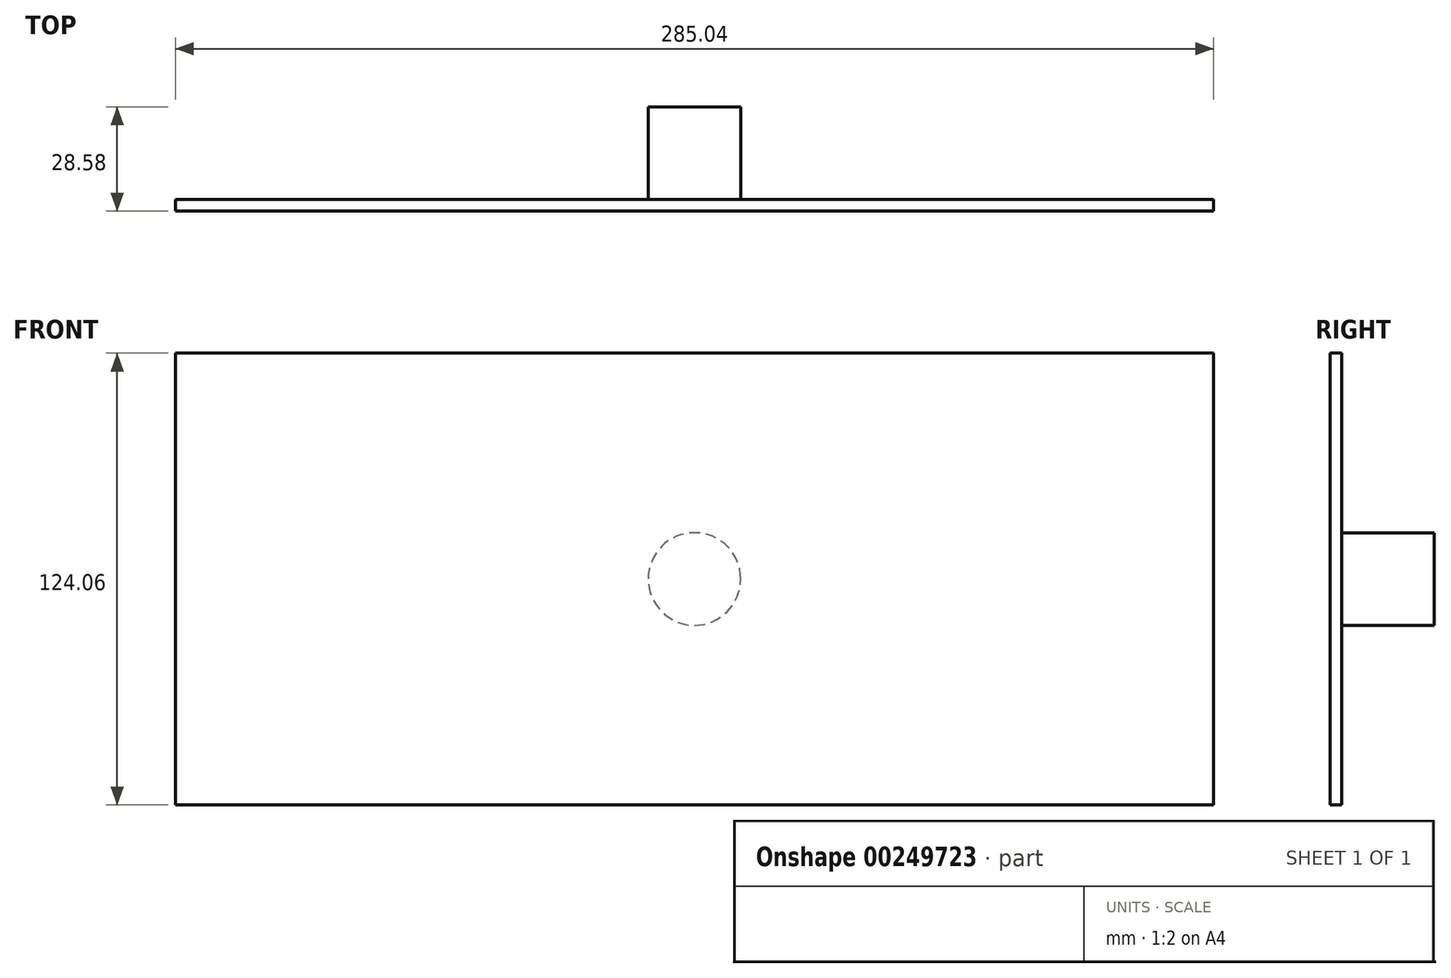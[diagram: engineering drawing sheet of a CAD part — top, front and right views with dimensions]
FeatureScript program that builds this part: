
annotation { "Feature Type Name" : "Feature", "Feature Type Description" : "" }
export const myFeature = defineFeature(function(context is Context, id is Id, definition is map)
    precondition{}
    {
        {
            var Q0;
            Q0=qCreatedBy(makeId("Front.planeOp"),FACE);
            var sketch = newSketch(context, id + "F0", { "sketchPlane" : qUnion([Q0])});
            skLineSegment(sketch, "E0.bottom", {"start": v(142.52, -62.03) * mm, "end": v(-142.52, -62.03) * mm});
            skLineSegment(sketch, "E0.top", {"start": v(142.52, 62.03) * mm, "end": v(-142.52, 62.03) * mm});
            skLineSegment(sketch, "E0.left", {"start": v(142.52, -62.03) * mm, "end": v(142.52, 62.03) * mm});
            skLineSegment(sketch, "E0.right", {"start": v(-142.52, -62.03) * mm, "end": v(-142.52, 62.03) * mm});
            skPoint(sketch, "E0.middle", {"position": v(0, 0) * mm});
            skSolve(sketch);
        }
        {
            var Q0;
            Q0 = qSketchRegion(id + "F0", true);
            extrude(context, id + "F1", {"entities" : qUnion([Q0]), "oppositeDirection" : true, "depth" : 3.17 * mm});
        }
        {
            var Q0;
            Q0=makeQuery(id+"F1.opExtrude","CAP_FACE",FACE,{"disambiguationData":[OSD([sQuery(id+"F0.wireOp",EDGE,"E0.bottom"),sQuery(id+"F0.wireOp",EDGE,"E0.top"),sQuery(id+"F0.wireOp",EDGE,"E0.left"),sQuery(id+"F0.wireOp",EDGE,"E0.right")])],"isStart":false});
            var sketch = newSketch(context, id + "F2", { "sketchPlane" : qUnion([Q0])});
            skCircle(sketch, "E1", {"center": v(0, 0) * mm, "radius": 12.7 * mm});
            skSolve(sketch);
        }
        {
            var Q0;
            Q0 = qSketchRegion(id + "F2", true);
            extrude(context, id + "F3", {"entities" : qUnion([Q0]), "operationType" : NewBodyOperationType.ADD, "depth" : 25.4 * mm});
        }
    });
